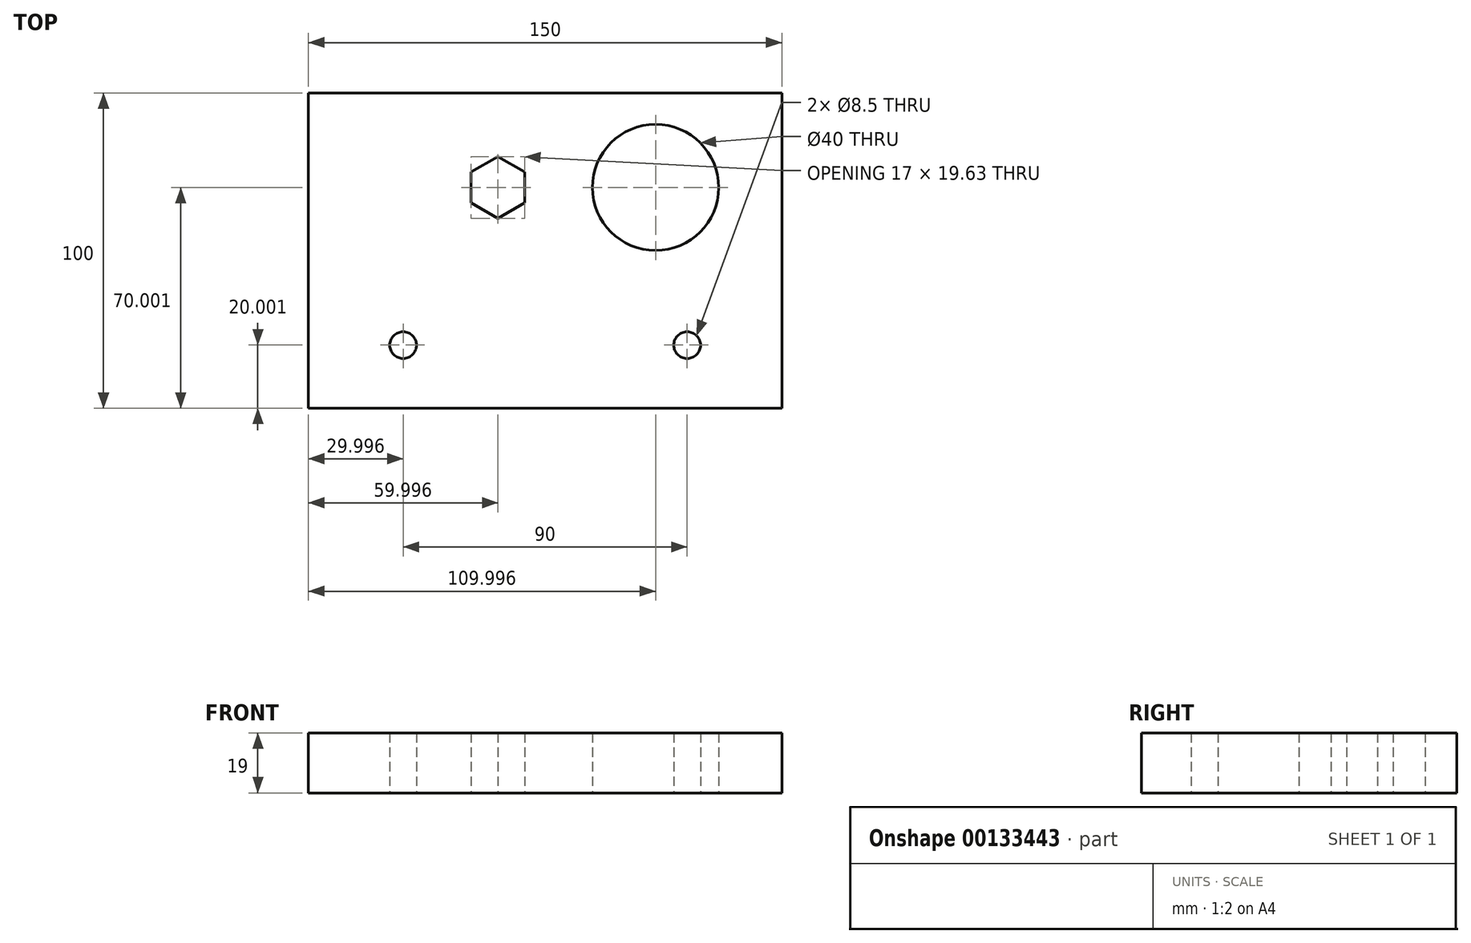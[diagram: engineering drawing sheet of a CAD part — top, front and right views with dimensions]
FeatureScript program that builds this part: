
annotation { "Feature Type Name" : "Feature", "Feature Type Description" : "" }
export const myFeature = defineFeature(function(context is Context, id is Id, definition is map)
    precondition{}
    {
        {
            var Q0;
            Q0=qCreatedBy(makeId("Top.planeOp"),FACE);
            var sketch = newSketch(context, id + "F0", { "sketchPlane" : qUnion([Q0])});
            skLineSegment(sketch, "E0.bottom", {"start": v(-76.58, -39.86) * mm, "end": v(73.42, -39.86) * mm});
            skLineSegment(sketch, "E0.top", {"start": v(-76.58, 60.14) * mm, "end": v(73.42, 60.14) * mm});
            skLineSegment(sketch, "E0.left", {"start": v(-76.58, -39.86) * mm, "end": v(-76.58, 60.14) * mm});
            skLineSegment(sketch, "E0.right", {"start": v(73.42, -39.86) * mm, "end": v(73.42, 60.14) * mm});
            skLineSegment(sketch, "E1", {"start": v(-76.58, -19.86) * mm, "end": v(73.42, -19.86) * mm, "construction": true});
            skCircle(sketch, "E2", {"center": v(33.42, 30.14) * mm, "radius": 20 * mm});
            skLineSegment(sketch, "E3", {"start": v(-76.58, 0.14) * mm, "end": v(73.42, 0.14) * mm, "construction": true});
            skCircle(sketch, "E4.cCircle", {"center": v(-16.58, 30.14) * mm, "radius": 8.5 * mm, "construction": true});
            skLineSegment(sketch, "E4.0", {"start": v(-8.08, 35.05) * mm, "end": v(-8.08, 25.23) * mm});
            skLineSegment(sketch, "E4.1", {"start": v(-8.08, 25.23) * mm, "end": v(-16.58, 20.33) * mm});
            skLineSegment(sketch, "E4.2", {"start": v(-16.58, 20.33) * mm, "end": v(-25.08, 25.23) * mm});
            skLineSegment(sketch, "E4.3", {"start": v(-25.08, 25.23) * mm, "end": v(-25.08, 35.05) * mm});
            skLineSegment(sketch, "E4.4", {"start": v(-25.08, 35.05) * mm, "end": v(-16.58, 39.96) * mm});
            skLineSegment(sketch, "E4.5", {"start": v(-16.58, 39.96) * mm, "end": v(-8.08, 35.05) * mm});
            skPoint(sketch, "E4.0.midPoint", {"position": v(-8.08, 30.14) * mm});
            skCircle(sketch, "E5", {"center": v(-46.58, -19.86) * mm, "radius": 4.25 * mm});
            skCircle(sketch, "E6", {"center": v(43.42, -19.86) * mm, "radius": 4.25 * mm});
            skSolve(sketch);
        }
        {
            var Q0;
            Q0=makeQuery(id+"F0.imprint","IMPRINT",FACE,{"disambiguationData":[TD([[makeQuery(id+"F0.imprint","IMPRINT",EDGE,{"derivedFrom":sQuery(id+"F0.wireOp",EDGE,"E0.bottom")}),1.0]])]});
            extrude(context, id + "F1", {"entities" : qUnion([Q0]), "depth" : 19 * mm});
        }
    });
